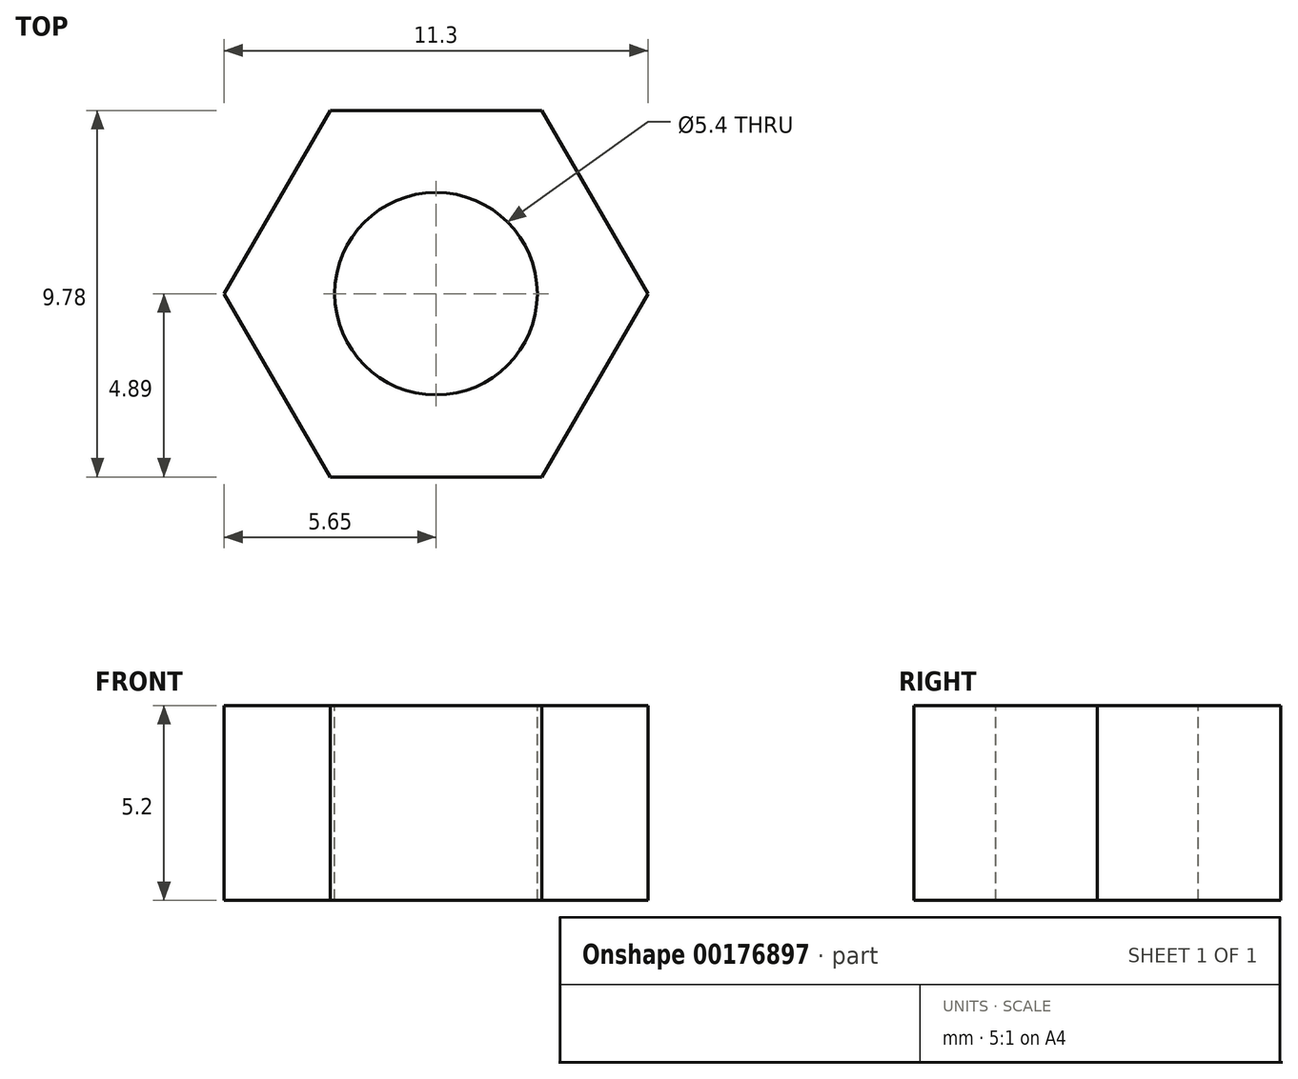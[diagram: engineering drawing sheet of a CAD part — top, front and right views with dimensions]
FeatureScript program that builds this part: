
annotation { "Feature Type Name" : "Feature", "Feature Type Description" : "" }
export const myFeature = defineFeature(function(context is Context, id is Id, definition is map)
    precondition{}
    {
        {
            var Q0;
            Q0=qCreatedBy(makeId("Top.planeOp"),FACE);
            var sketch = newSketch(context, id + "F0", { "sketchPlane" : qUnion([Q0])});
            skCircle(sketch, "E0.cCircle", {"center": v(0, 0) * mm, "radius": 4.9 * mm, "construction": true});
            skLineSegment(sketch, "E0.0", {"start": v(-2.82, 4.89) * mm, "end": v(2.82, 4.89) * mm});
            skLineSegment(sketch, "E0.1", {"start": v(2.82, 4.89) * mm, "end": v(5.65, 0) * mm});
            skLineSegment(sketch, "E0.2", {"start": v(5.65, 0) * mm, "end": v(2.82, -4.89) * mm});
            skLineSegment(sketch, "E0.3", {"start": v(2.82, -4.89) * mm, "end": v(-2.82, -4.89) * mm});
            skLineSegment(sketch, "E0.4", {"start": v(-2.82, -4.9) * mm, "end": v(-5.65, 0) * mm});
            skLineSegment(sketch, "E0.5", {"start": v(-5.65, 0) * mm, "end": v(-2.82, 4.89) * mm});
            skPoint(sketch, "E0.0.midPoint", {"position": v(0, 4.89) * mm});
            skSolve(sketch);
        }
        {
            var Q0;
            Q0=makeQuery(id+"F0.imprint","IMPRINT",FACE,{"disambiguationData":[TD([[makeQuery(id+"F0.imprint","IMPRINT",EDGE,{"derivedFrom":sQuery(id+"F0.wireOp",EDGE,"E0.0")}),-1.0]])]});
            extrude(context, id + "F1", {"entities" : qUnion([Q0]), "depth" : 5.2 * mm});
        }
        {
            var Q0;
            Q0=makeQuery(id+"F1.opExtrude","CAP_FACE",FACE,{"disambiguationData":[OSD([sQuery(id+"F0.wireOp",EDGE,"E0.0"),sQuery(id+"F0.wireOp",EDGE,"E0.1"),sQuery(id+"F0.wireOp",EDGE,"E0.2"),sQuery(id+"F0.wireOp",EDGE,"E0.3"),sQuery(id+"F0.wireOp",EDGE,"E0.4"),sQuery(id+"F0.wireOp",EDGE,"E0.5")])],"isStart":false});
            var sketch = newSketch(context, id + "F2", { "sketchPlane" : qUnion([Q0])});
            skCircle(sketch, "E1", {"center": v(0, 0) * mm, "radius": 2.7 * mm});
            skSolve(sketch);
        }
        {
            var Q0;
            Q0=makeQuery(id+"F2.imprint","IMPRINT",FACE,{"disambiguationData":[TD([[makeQuery(id+"F2.imprint","IMPRINT",EDGE,{"derivedFrom":sQuery(id+"F2.wireOp",EDGE,"E1")}),1.0]])]});
            extrude(context, id + "F3", {"entities" : qUnion([Q0]), "operationType" : NewBodyOperationType.REMOVE, "endBound" : BoundingType.UP_TO_NEXT, "oppositeDirection" : true, "depth" : 25 * mm});
        }
        {
            var Q0;
            Q0=makeQuery(id+"F1.opExtrude","CAP_FACE",FACE,{"disambiguationData":[OSD([sQuery(id+"F0.wireOp",EDGE,"E0.0"),sQuery(id+"F0.wireOp",EDGE,"E0.1"),sQuery(id+"F0.wireOp",EDGE,"E0.2"),sQuery(id+"F0.wireOp",EDGE,"E0.3"),sQuery(id+"F0.wireOp",EDGE,"E0.4"),sQuery(id+"F0.wireOp",EDGE,"E0.5")])],"isStart":false});
            var sketch = newSketch(context, id + "F4", { "sketchPlane" : qUnion([Q0])});
            skCircle(sketch, "E2", {"center": v(0, 0) * mm, "radius": 3 * mm, "construction": true});
            skSolve(sketch);
        }
    });
